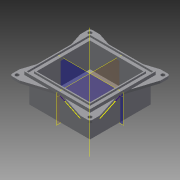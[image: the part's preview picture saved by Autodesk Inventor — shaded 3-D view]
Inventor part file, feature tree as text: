
AUTODESK INVENTOR PART (.ipt)
format: ipt  version: 2015 (Build 190159000, 159)  size: 266,752 bytes
history: native  units: in
note: dims shown in document units (in); Inventor stores cm internally (conversion verified against a paired STEP export)
features: sketch x8, extrude x5, plane x4, projected_geometry x4, mirror x2, hole x1, fillet x1, rib x1
ambient origin geometry x8: Origin, YZ Plane, XZ Plane, XY Plane, X Axis, Y Axis, Z Axis, Center Point
bodies: Solid1 (feature_tree)
feature tree (26):
  extrude  "Extrusion1"  Depth=1.9685in
  extrude  "Extrusion2"  Depth=0.0394in
  extrude  "Extrusion3"  Depth=0.0394in
  extrude  "Extrusion4"  Depth=0.0394in
  extrude  "Extrusion5"  Depth=0.0394in TaperAngle=0.0deg
  hole  "Hole1"  [1 undecoded]
  fillet  "Fillet1"  Radius=0.0591in
  sketch  "Sketch7"  dims[d17=0.315in]
  plane  "Work Plane1"
  rib  "Rib1"
  plane  "Work Plane2"
  plane  "Work Plane3"
  mirror  "Mirror1"
  mirror  "Mirror2"
  sketch  "Sketch1"  dims[d0=1.9685in d1=1.9685in]
  sketch  "Sketch2"  dims[d2=0.0394in d3=0.0in d4=0.0394in]
  projected_geometry  "Projected Loop1"
  sketch  "Sketch3"  dims[d5=0.7874in d6=0.0in d7=0.0394in]
  projected_geometry  "Projected Loop2"
  sketch  "Sketch4"  dims[d8=0.0394in d9=0.0394in]
  projected_geometry  "Projected Loop3"
  sketch  "Sketch5"  dims[d10=0.0394in d11=0.0394in d12=0.0in]
  sketch  "Sketch6"  dims[d13=0.0394in d14=0.0394in d15=0.0591in d16=0.0in]
  projected_geometry  "Projected Loop4"
  sketch  "Sketch8"  dims[d18=0.315in d19=0.0787in d20=0.0in d21=0.2362in d22=0.1181in d23=0.2362in d24=0.1575in d25=0.0787in d26=90.0deg d27=0.315in d28=0.8108in d29=1.9685in d30=0.0787in d31=0.1181in d32=0.0394in d33=0.1181in d34=0.2362in d35=0.1181in d36=0.1181in d37=45.0deg d38=135.0deg d39=0.0394in d40=0.0787in d41=0.0in d42=0.0in d43=0.0394in d44=0.0394in d45=-0.9843in d46=-0.9843in]
  plane  "Work Plane4"
note: 1 required parameter value undecoded (feature->parameter linkage not recoverable at this tier; creation-order binding heuristic only, values carry confidence <= 0.55)
